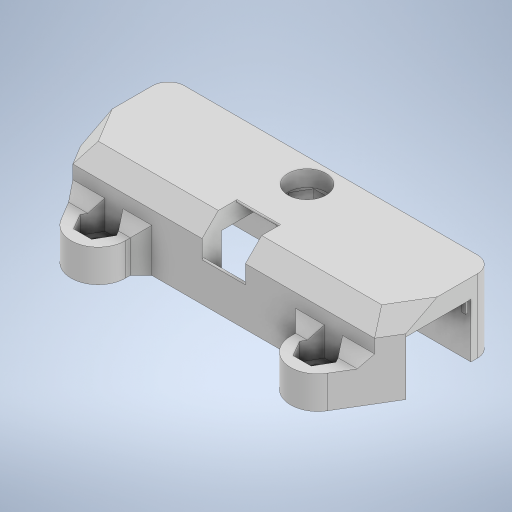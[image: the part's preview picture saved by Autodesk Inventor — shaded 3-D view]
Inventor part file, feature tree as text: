
AUTODESK INVENTOR PART (.ipt)
format: ipt  version: 2023 (Build 270158000, 158)  size: 510,464 bytes
history: native  units: mm
features: extrude x12, sketch x10, projected_geometry x9, chamfer x3, fillet x2, other x1
ambient origin geometry x8: Origin, YZ Plane, XZ Plane, XY Plane, X Axis, Y Axis, Z Axis, Center Point
bodies: Body1 (feature_tree)
feature tree (37):
  other  "Bryła1"
  extrude  "Wyciągnięcie proste1"  Depth=10.0mm
  extrude  "Wyciągnięcie proste2"  Depth=10.0mm
  extrude  "Wyciągnięcie proste3"  Depth=10.0mm
  sketch  "Szkic4"
  extrude  "Wyciągnięcie proste4"  Depth=10.0mm TaperAngle=0.0deg
  extrude  "Wyciągnięcie proste5"  Depth=3.5mm TaperAngle=0.0deg
  extrude  "Wyciągnięcie proste6"  Depth=4.0mm
  sketch  "Szkic6"
  extrude  "Wyciągnięcie proste7"  Depth=3.5mm TaperAngle=0.0deg
  extrude  "Wyciągnięcie proste8"  Depth=5.8mm
  extrude  "Wyciągnięcie proste9"  Depth=5.8mm
  extrude  "Wyciągnięcie proste10"  Depth=7.5mm TaperAngle=0.0deg
  extrude  "Wyciągnięcie proste12"  Depth=10.8mm TaperAngle=0.0deg
  chamfer  "Faza1"  [1 undecoded]
  fillet  "Zaokrąglenie3"  Radius=5.8mm
  fillet  "Zaokrąglenie4"  Radius=7.0mm
  chamfer  "Faza2"  Distance=3.0mm
  chamfer  "Faza3"  Distance=6.0mm
  extrude  "Wyciągnięcie proste13"  Depth=0.7mm
  sketch  "Szkic1"
  sketch  "Szkic2"
  projected_geometry  "Pętla rzutowana1"
  projected_geometry  "Pętla rzutowana2"
  projected_geometry  "Pętla rzutowana3"
  sketch  "Szkic3"
  projected_geometry  "Pętla rzutowana4"
  projected_geometry  "Pętla rzutowana5"
  projected_geometry  "Pętla rzutowana6"
  sketch  "Szkic5"
  projected_geometry  "Pętla rzutowana7"
  sketch  "Szkic7"
  projected_geometry  "Pętla rzutowana8"
  sketch  "Szkic8"
  sketch  "Szkic10"
  sketch  "Szkic11"
  projected_geometry  "Pętla rzutowana9"
note: 1 required parameter value undecoded (feature->parameter linkage not recoverable at this tier; creation-order binding heuristic only, values carry confidence <= 0.55)
